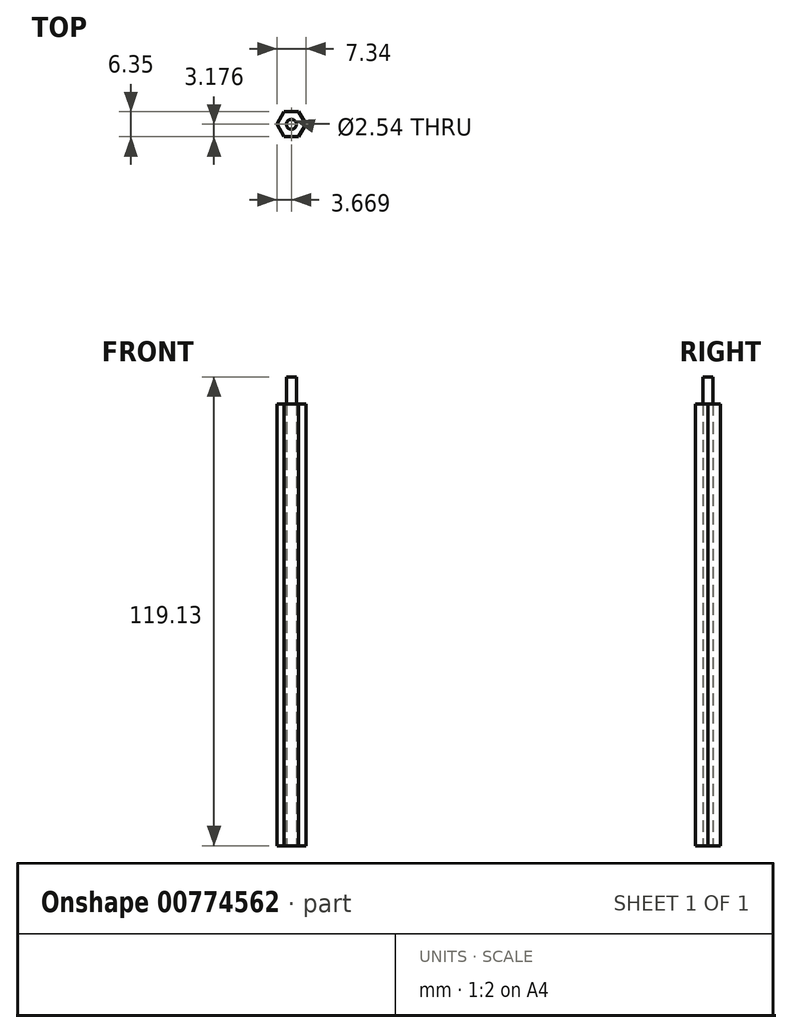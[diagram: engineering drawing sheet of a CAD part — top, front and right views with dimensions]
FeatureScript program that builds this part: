
annotation { "Feature Type Name" : "Feature", "Feature Type Description" : "" }
export const myFeature = defineFeature(function(context is Context, id is Id, definition is map)
    precondition{}
    {
        {
            var Q0;
            Q0=qCreatedBy(makeId("Top.planeOp"),FACE);
            var sketch = newSketch(context, id + "F0", { "sketchPlane" : qUnion([Q0])});
            skCircle(sketch, "E0.cCircle", {"center": v(-22.17, -4.62) * mm, "radius": 3.18 * mm, "construction": true});
            skLineSegment(sketch, "E0.0", {"start": v(-20.34, -7.8) * mm, "end": v(-24, -7.8) * mm});
            skLineSegment(sketch, "E0.1", {"start": v(-24, -7.8) * mm, "end": v(-25.84, -4.62) * mm});
            skLineSegment(sketch, "E0.2", {"start": v(-25.84, -4.62) * mm, "end": v(-24, -1.45) * mm});
            skLineSegment(sketch, "E0.3", {"start": v(-24, -1.45) * mm, "end": v(-20.34, -1.45) * mm});
            skLineSegment(sketch, "E0.4", {"start": v(-20.34, -1.45) * mm, "end": v(-18.5, -4.62) * mm});
            skLineSegment(sketch, "E0.5", {"start": v(-18.5, -4.62) * mm, "end": v(-20.34, -7.8) * mm});
            skPoint(sketch, "E0.0.midPoint", {"position": v(-22.17, -7.8) * mm});
            skCircle(sketch, "E1", {"center": v(-22.17, -4.62) * mm, "radius": 1.27 * mm});
            skSolve(sketch);
        }
        {
            var Q0;
            Q0=makeQuery(id+"F0.imprint","IMPRINT",FACE,{"disambiguationData":[TD([[makeQuery(id+"F0.imprint","IMPRINT",EDGE,{"derivedFrom":sQuery(id+"F0.wireOp",EDGE,"E0.0")}),-1.0]])]});
            extrude(context, id + "F1", {"entities" : qUnion([Q0]), "depth" : 112.27 * mm, "offsetDistance" : 25.4 * mm});
        }
        {
            var Q0;
            Q0=makeQuery(id+"F1.opExtrude","CAP_FACE",FACE,{"disambiguationData":[OSD([sQuery(id+"F0.wireOp",EDGE,"E0.0"),sQuery(id+"F0.wireOp",EDGE,"E0.1"),sQuery(id+"F0.wireOp",EDGE,"E0.2"),sQuery(id+"F0.wireOp",EDGE,"E0.3"),sQuery(id+"F0.wireOp",EDGE,"E0.4"),sQuery(id+"F0.wireOp",EDGE,"E0.5"),sQuery(id+"F0.wireOp",EDGE,"E1")])],"isStart":true});
            var sketch = newSketch(context, id + "F2", { "sketchPlane" : qUnion([Q0])});
            skCircle(sketch, "E2", {"center": v(-22.17, 4.62) * mm, "radius": 1.27 * mm});
            skSolve(sketch);
        }
        {
            var Q0;
            Q0=makeQuery(id+"F2.imprint","IMPRINT",FACE,{"disambiguationData":[TD([[makeQuery(id+"F2.imprint","IMPRINT",EDGE,{"derivedFrom":sQuery(id+"F2.wireOp",EDGE,"E2")}),1.0]])]});
            var Q1;
            Q1=sQuery(id+"F2.wireOp",EDGE,"E2");
            extrude(context, id + "F3", {"entities" : qUnion([Q0]), "surfaceEntities" : qUnion([Q1]), "oppositeDirection" : true, "depth" : 119.13 * mm, "offsetDistance" : 25.4 * mm});
        }
    });
